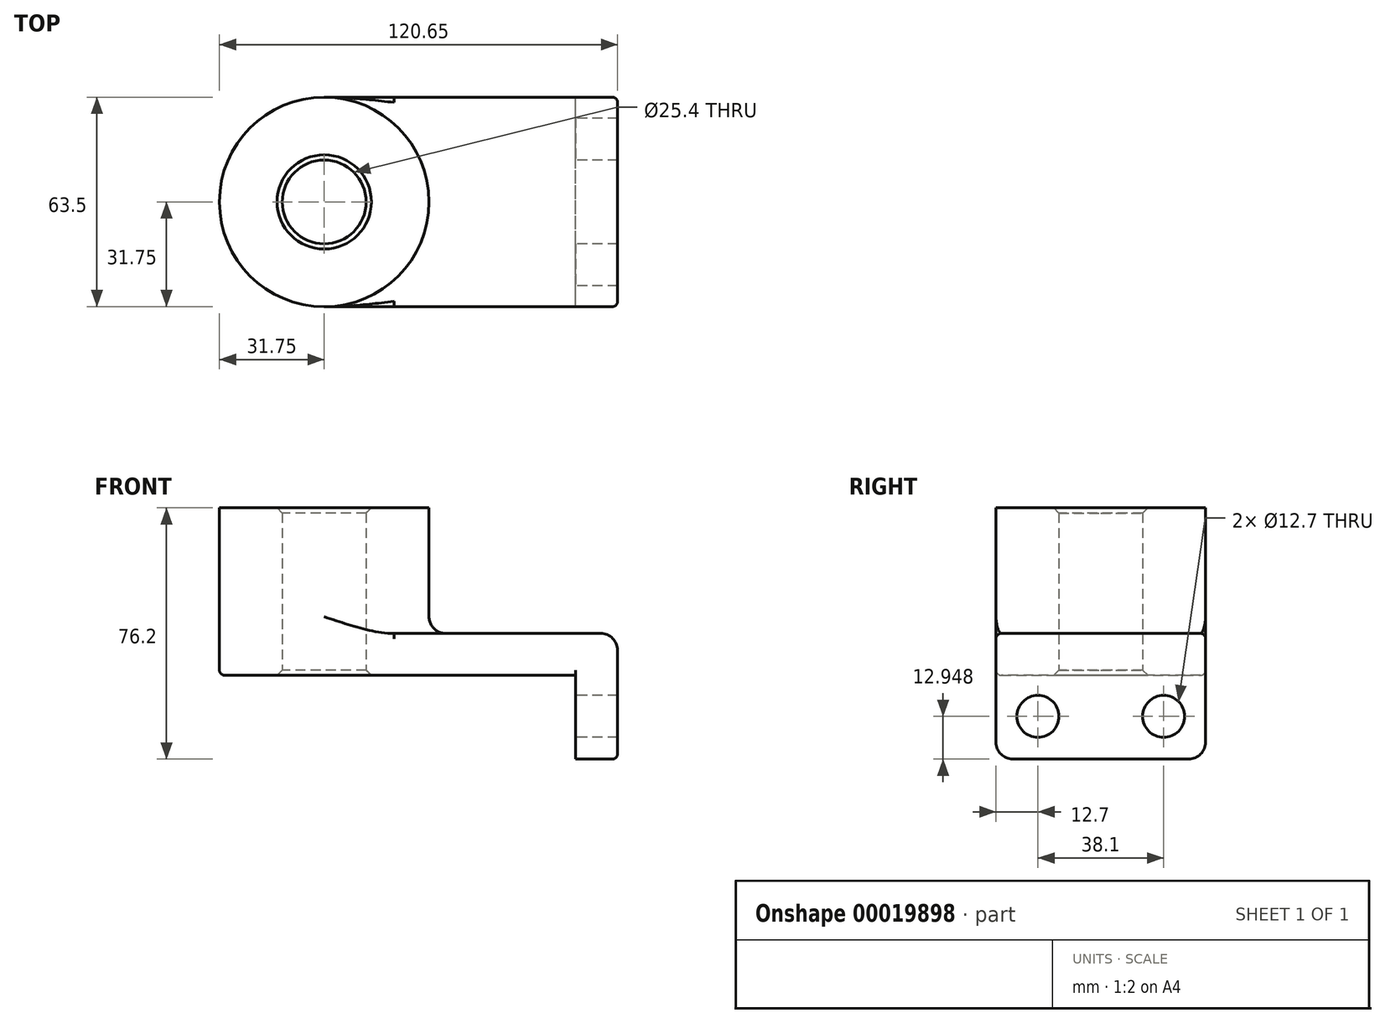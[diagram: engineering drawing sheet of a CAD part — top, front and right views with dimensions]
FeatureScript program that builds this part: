
annotation { "Feature Type Name" : "Feature", "Feature Type Description" : "" }
export const myFeature = defineFeature(function(context is Context, id is Id, definition is map)
    precondition{}
    {
        {
            var Q0;
            Q0=qCreatedBy(makeId("Top.planeOp"),FACE);
            var sketch = newSketch(context, id + "F0", { "sketchPlane" : qUnion([Q0])});
            skLineSegment(sketch, "E0.rect.bottom", {"start": v(-38.1, -31.75) * mm, "end": v(38.1, -31.75) * mm});
            skLineSegment(sketch, "E0.rect.top", {"start": v(-38.1, 31.75) * mm, "end": v(38.1, 31.75) * mm});
            skLineSegment(sketch, "E0.rect.left", {"start": v(-38.1, -31.75) * mm, "end": v(-38.1, 31.75) * mm});
            skLineSegment(sketch, "E0.rect.right", {"start": v(38.1, -31.75) * mm, "end": v(38.1, 31.75) * mm});
            skPoint(sketch, "E0.rect.middle", {"position": v(0, 0) * mm});
            skCircle(sketch, "E1", {"center": v(-38.1, 0) * mm, "radius": 31.75 * mm});
            skCircle(sketch, "E2", {"center": v(-38.1, 0) * mm, "radius": 12.7 * mm});
            skSolve(sketch);
        }
        {
            var Q0;
            Q0 = qSketchRegion(id + "F0", true);
            extrude(context, id + "F1", {"entities" : qUnion([Q0]), "depth" : 12.7 * mm});
        }
        {
            var Q0;
            {var subQ0=sQuery(id+"F0.wireOp",EDGE,"E2");var subQ1=sQuery(id+"F0.wireOp",EDGE,"E0.rect.left");var subQ3=makeQuery(id+"F0.imprint","INTERSECT",VERTEX,{"disambiguationData":[OD(0.0)],"derivedFrom":[subQ1,subQ0]});Q0=makeQuery(id+"F0.imprint","IMPRINT",FACE,{"disambiguationData":[TD([[makeQuery(id+"F0.imprint","IMPRINT",EDGE,{"disambiguationData":[TD([[subQ3,1.0]])],"derivedFrom":subQ0}),-1.0]])]});}
            var Q1;
            {var subQ0=sQuery(id+"F0.wireOp",EDGE,"E2");var subQ1=sQuery(id+"F0.wireOp",EDGE,"E0.rect.left");var subQ3=makeQuery(id+"F0.imprint","INTERSECT",VERTEX,{"disambiguationData":[OD(0.0)],"derivedFrom":[subQ1,subQ0]});Q1=makeQuery(id+"F0.imprint","IMPRINT",FACE,{"disambiguationData":[TD([[makeQuery(id+"F0.imprint","IMPRINT",EDGE,{"disambiguationData":[TD([[subQ3,-1.0]])],"derivedFrom":subQ0}),-1.0]])]});}
            extrude(context, id + "F2", {"entities" : qUnion([Q0, Q1]), "operationType" : NewBodyOperationType.ADD, "depth" : 50.8 * mm});
        }
        {
            var Q0;
            Q0=makeQuery(id+"F1.opExtrude","SWEPT_FACE",FACE,{"disambiguationData":[OSD([sQuery(id+"F0.wireOp",EDGE,"E0.rect.right")])]});
            var sketch = newSketch(context, id + "F3", { "sketchPlane" : qUnion([Q0])});
            skLineSegment(sketch, "E3.bottom", {"start": v(-31.75, 12.7) * mm, "end": v(31.75, 12.7) * mm});
            skLineSegment(sketch, "E3.top", {"start": v(-31.75, -25.4) * mm, "end": v(31.75, -25.4) * mm});
            skLineSegment(sketch, "E3.left", {"start": v(-31.75, 12.7) * mm, "end": v(-31.75, -25.4) * mm});
            skLineSegment(sketch, "E3.right", {"start": v(31.75, 12.7) * mm, "end": v(31.75, -25.4) * mm});
            skCircle(sketch, "E4", {"center": v(-19.05, -12.45) * mm, "radius": 6.35 * mm});
            skLineSegment(sketch, "E5", {"start": v(0, 0) * mm, "end": v(0, -25.4) * mm});
            skCircle(sketch, "E6.MirrorC", {"center": v(19.05, -12.45) * mm, "radius": 6.35 * mm});
            skSolve(sketch);
        }
        {
            var Q0;
            Q0 = qSketchRegion(id + "F3", true);
            extrude(context, id + "F4", {"entities" : qUnion([Q0]), "operationType" : NewBodyOperationType.ADD, "depth" : 12.7 * mm});
        }
        {
            var Q0;
            {var subQ0=sQuery(id+"F0.wireOp",EDGE,"E1");Q0=makeQuery(id+"F2.boolean.opBoolean","INTERSECT",EDGE,{"derivedFrom":[makeQuery(id+"F1.opExtrude","CAP_FACE",FACE,{"disambiguationData":[OSD([sQuery(id+"F0.wireOp",EDGE,"E0.rect.bottom"),sQuery(id+"F0.wireOp",EDGE,"E0.rect.top"),sQuery(id+"F0.wireOp",EDGE,"E0.rect.right"),subQ0,sQuery(id+"F0.wireOp",EDGE,"E2")])],"isStart":false}),makeQuery(id+"F2.opExtrude","SWEPT_FACE",FACE,{"disambiguationData":[OSD([subQ0])]})]});}
            var Q1;
            Q1=makeQuery(id+"F4.opExtrude","SWEPT_EDGE",EDGE,{"disambiguationData":[OSD([sQuery(id+"F3.wireOp",EDGE,"E3.top"),sQuery(id+"F3.wireOp",EDGE,"E3.left")])]});
            var Q2;
            Q2=makeQuery(id+"F4.opExtrude","SWEPT_EDGE",EDGE,{"disambiguationData":[OSD([sQuery(id+"F3.wireOp",EDGE,"E3.top"),sQuery(id+"F3.wireOp",EDGE,"E3.right")])]});
            var Q3;
            Q3=makeQuery(id+"F4.opExtrude","CAP_EDGE",EDGE,{"disambiguationData":[OSD([sQuery(id+"F3.wireOp",EDGE,"E3.bottom")])],"isStart":false});
            fillet(context, id + "F5", {"entities" : qUnion([Q0, Q1, Q2, Q3]), "radius" : 5.08 * mm, "tangentPropagation" : true, "allowEdgeOverflow" : false});
        }
        {
            var Q0;
            Q0=makeQuery(id+"F4.boolean.opBoolean","MERGE",EDGE,{"derivedFrom":[makeQuery(id+"F1.opExtrude","CAP_EDGE",EDGE,{"disambiguationData":[OSD([sQuery(id+"F0.wireOp",EDGE,"E0.rect.bottom")])],"isStart":false}),makeQuery(id+"F4.opExtrude","SWEPT_EDGE",EDGE,{"disambiguationData":[OSD([sQuery(id+"F3.wireOp",EDGE,"E3.bottom"),sQuery(id+"F3.wireOp",EDGE,"E3.left")])]})]});
            var Q1;
            Q1=makeQuery(id+"F1.opExtrude","CAP_EDGE",EDGE,{"disambiguationData":[OSD([sQuery(id+"F0.wireOp",EDGE,"E0.rect.bottom")])],"isStart":true});
            var Q2;
            Q2=makeQuery(id+"F1.opExtrude","CAP_EDGE",EDGE,{"disambiguationData":[OSD([sQuery(id+"F0.wireOp",EDGE,"E0.rect.right")])],"isStart":true});
            fillet(context, id + "F6", {"entities" : qUnion([Q0, Q1, Q2]), "radius" : 1.59 * mm, "tangentPropagation" : true, "allowEdgeOverflow" : false});
        }
        {
            var Q0;
            {var subQ0=sQuery(id+"F0.wireOp",EDGE,"E2");Q0=makeQuery(id+"F2.boolean.opBoolean","MERGE",FACE,{"derivedFrom":[makeQuery(id+"F1.opExtrude","SWEPT_FACE",FACE,{"disambiguationData":[OSD([subQ0])]}),makeQuery(id+"F2.opExtrude","SWEPT_FACE",FACE,{"disambiguationData":[OSD([subQ0])]})]});}
            chamfer(context, id + "F7", {"entities" : qUnion([Q0]), "width" : 1.59 * mm, "tangentPropagation" : true});
        }
    });
